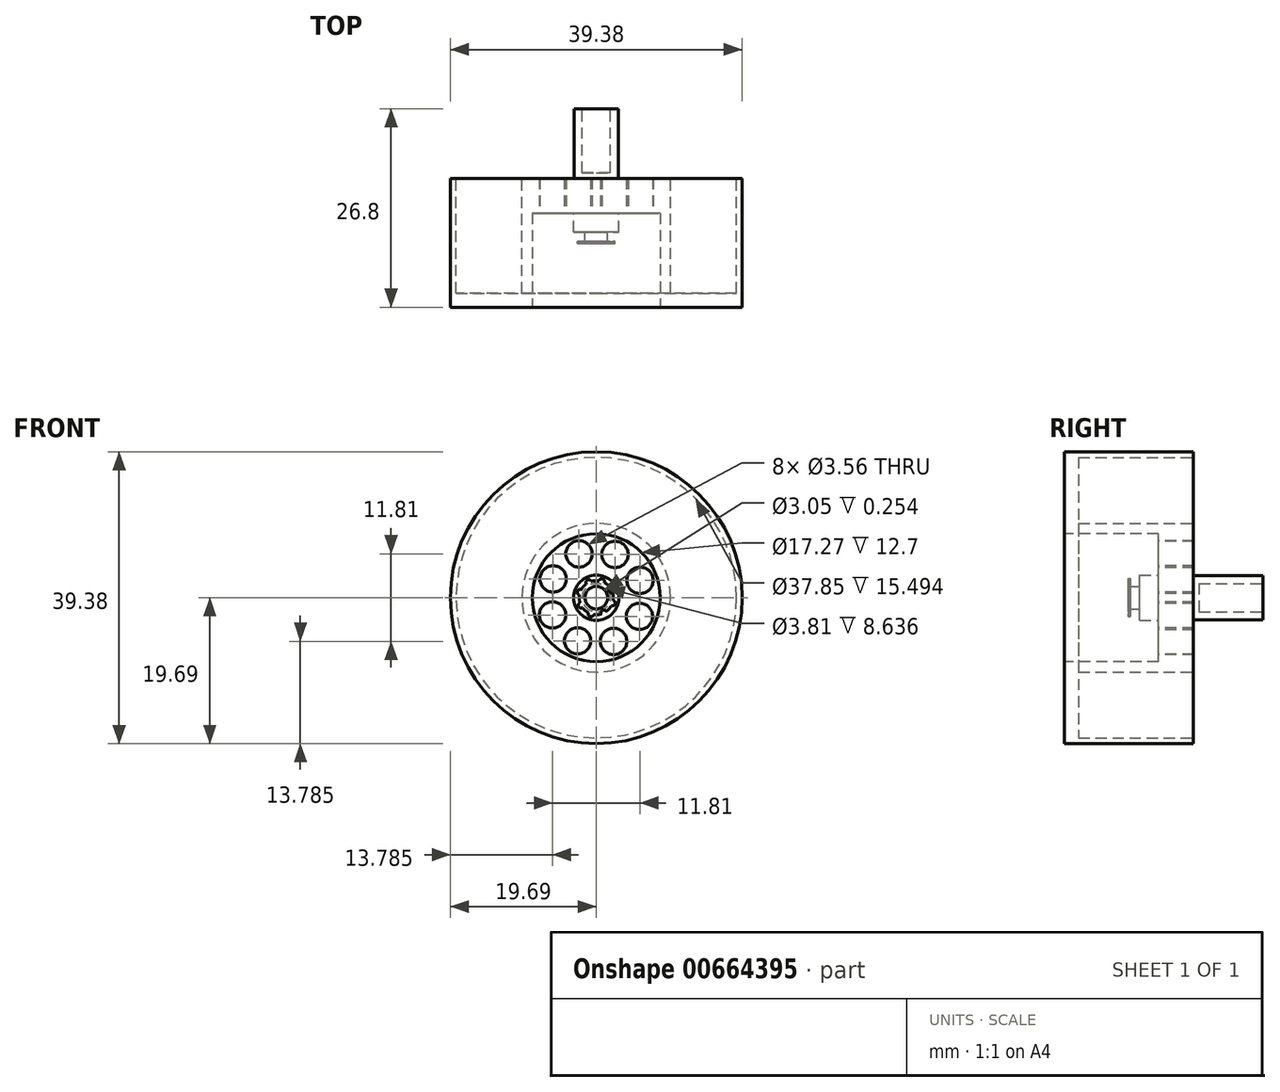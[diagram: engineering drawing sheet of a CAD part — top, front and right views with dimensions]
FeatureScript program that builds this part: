
annotation { "Feature Type Name" : "Feature", "Feature Type Description" : "" }
export const myFeature = defineFeature(function(context is Context, id is Id, definition is map)
    precondition{}
    {
        {
            var Q0;
            Q0=qCreatedBy(makeId("Front.planeOp"),FACE);
            var sketch = newSketch(context, id + "F0", { "sketchPlane" : qUnion([Q0])});
            skCircle(sketch, "E0", {"center": v(0, 0) * mm, "radius": 19.69 * mm});
            skSolve(sketch);
        }
        {
            var Q0;
            Q0 = qSketchRegion(id + "F0", true);
            extrude(context, id + "F1", {"entities" : qUnion([Q0]), "oppositeDirection" : true, "depth" : 17.4 * mm, "offsetDistance" : 25.4 * mm});
        }
        {
            var Q0;
            Q0=qCreatedBy(makeId("Front.planeOp"),FACE);
            var sketch = newSketch(context, id + "F2", { "sketchPlane" : qUnion([Q0])});
            skCircle(sketch, "E1", {"center": v(0, 0) * mm, "radius": 7.62 * mm});
            skSolve(sketch);
        }
        {
            var Q0;
            Q0 = qSketchRegion(id + "F2", true);
            extrude(context, id + "F3", {"entities" : qUnion([Q0]), "operationType" : NewBodyOperationType.REMOVE, "oppositeDirection" : true, "depth" : 13.2 * mm, "offsetDistance" : 25.4 * mm});
        }
        {
            var Q0;
            Q0 = qSketchRegion(id + "F0", true);
            extrude(context, id + "F4", {"entities" : qUnion([Q0]), "operationType" : NewBodyOperationType.ADD, "oppositeDirection" : true, "depth" : 16.5 * mm, "offsetDistance" : 25.4 * mm});
        }
        {
            var Q0;
            {var subQ0=sQuery(id+"F0.wireOp",EDGE,"E0");Q0=makeQuery(id+"F4.boolean.opBoolean","MERGE",FACE,{"derivedFrom":[makeQuery(id+"F1.opExtrude","CAP_FACE",FACE,{"disambiguationData":[OSD([subQ0])],"isStart":true}),makeQuery(id+"F4.opExtrude","CAP_FACE",FACE,{"disambiguationData":[OSD([subQ0])],"isStart":true})]});}
            var sketch = newSketch(context, id + "F5", { "sketchPlane" : qUnion([Q0])});
            skCircle(sketch, "E2", {"center": v(0, 0) * mm, "radius": 8.64 * mm});
            skSolve(sketch);
        }
        {
            var Q0;
            Q0 = qSketchRegion(id + "F5", true);
            extrude(context, id + "F6", {"entities" : qUnion([Q0]), "operationType" : NewBodyOperationType.REMOVE, "oppositeDirection" : true, "depth" : 12.7 * mm, "offsetDistance" : 25.4 * mm});
        }
        {
            var Q0;
            Q0=makeQuery(id+"F6.boolean.opBoolean","COPY",FACE,{"derivedFrom":makeQuery(id+"F6.opExtrude","CAP_FACE",FACE,{"disambiguationData":[OSD([sQuery(id+"F5.wireOp",EDGE,"E2")])],"isStart":false})});
            var sketch = newSketch(context, id + "F7", { "sketchPlane" : qUnion([Q0])});
            skCircle(sketch, "E3", {"center": v(0, 0) * mm, "radius": 3.05 * mm});
            skSolve(sketch);
        }
        {
            var Q0;
            Q0 = qSketchRegion(id + "F7", true);
            extrude(context, id + "F8", {"entities" : qUnion([Q0]), "operationType" : NewBodyOperationType.ADD, "depth" : 2.54 * mm, "offsetDistance" : 25.4 * mm});
        }
        {
            var Q0;
            Q0=makeQuery(id+"F8.opExtrude","CAP_FACE",FACE,{"disambiguationData":[OSD([sQuery(id+"F7.wireOp",EDGE,"E3")])],"isStart":false});
            var sketch = newSketch(context, id + "F9", { "sketchPlane" : qUnion([Q0])});
            skCircle(sketch, "E4", {"center": v(0, 0) * mm, "radius": 1.52 * mm});
            skSolve(sketch);
        }
        {
            var Q0;
            Q0 = qSketchRegion(id + "F9", true);
            extrude(context, id + "F10", {"entities" : qUnion([Q0]), "operationType" : NewBodyOperationType.ADD, "depth" : 1.27 * mm, "offsetDistance" : 25.4 * mm});
        }
        {
            var Q0;
            Q0=makeQuery(id+"F10.opExtrude","CAP_FACE",FACE,{"disambiguationData":[OSD([sQuery(id+"F9.wireOp",EDGE,"E4")])],"isStart":false});
            var sketch = newSketch(context, id + "F11", { "sketchPlane" : qUnion([Q0])});
            skCircle(sketch, "E5", {"center": v(0, 0) * mm, "radius": 2.3 * mm});
            skCircle(sketch, "E6", {"center": v(-1.03, 2.06) * mm, "radius": 0.38 * mm});
            skCircle(sketch, "E7.1.0", {"center": v(-2.18, 0.73) * mm, "radius": 0.38 * mm});
            skCircle(sketch, "E7.2.0", {"center": v(-2.06, -1.03) * mm, "radius": 0.38 * mm});
            skCircle(sketch, "E7.3.0", {"center": v(-0.73, -2.18) * mm, "radius": 0.38 * mm});
            skCircle(sketch, "E7.4.0", {"center": v(1.03, -2.06) * mm, "radius": 0.38 * mm});
            skCircle(sketch, "E7.5.0", {"center": v(2.18, -0.73) * mm, "radius": 0.38 * mm});
            skCircle(sketch, "E7.6.0", {"center": v(2.06, 1.03) * mm, "radius": 0.38 * mm});
            skCircle(sketch, "E7.7.0", {"center": v(0.73, 2.18) * mm, "radius": 0.38 * mm});
            skSolve(sketch);
        }
        {
            var Q0;
            {var subQ0=sQuery(id+"F11.wireOp",EDGE,"E7.6.0");var subQ1=sQuery(id+"F11.wireOp",EDGE,"E5");var subQ2=makeQuery(id+"F11.imprint","INTERSECT",VERTEX,{"disambiguationData":[OD(0.0)],"derivedFrom":[subQ1,subQ0]});Q0=makeQuery(id+"F11.imprint","IMPRINT",FACE,{"disambiguationData":[TD([[makeQuery(id+"F11.imprint","IMPRINT",EDGE,{"disambiguationData":[TD([[subQ2,1.0]])],"derivedFrom":subQ1}),-1.0]])]});}
            var Q1;
            {var subQ0=sQuery(id+"F11.wireOp",EDGE,"E7.7.0");var subQ1=sQuery(id+"F11.wireOp",EDGE,"E5");var subQ2=makeQuery(id+"F11.imprint","INTERSECT",VERTEX,{"disambiguationData":[OD(0.0)],"derivedFrom":[subQ1,subQ0]});Q1=makeQuery(id+"F11.imprint","IMPRINT",FACE,{"disambiguationData":[TD([[makeQuery(id+"F11.imprint","IMPRINT",EDGE,{"disambiguationData":[TD([[subQ2,-1.0]])],"derivedFrom":subQ1}),-1.0]])]});}
            var Q2;
            {var subQ0=sQuery(id+"F11.wireOp",EDGE,"E6");var subQ1=sQuery(id+"F11.wireOp",EDGE,"E5");var subQ2=makeQuery(id+"F11.imprint","INTERSECT",VERTEX,{"disambiguationData":[OD(0.0)],"derivedFrom":[subQ1,subQ0]});Q2=makeQuery(id+"F11.imprint","IMPRINT",FACE,{"disambiguationData":[TD([[makeQuery(id+"F11.imprint","IMPRINT",EDGE,{"disambiguationData":[TD([[subQ2,-1.0]])],"derivedFrom":subQ1}),-1.0]])]});}
            var Q3;
            {var subQ0=sQuery(id+"F11.wireOp",EDGE,"E7.1.0");var subQ1=sQuery(id+"F11.wireOp",EDGE,"E5");var subQ2=makeQuery(id+"F11.imprint","INTERSECT",VERTEX,{"disambiguationData":[OD(0.0)],"derivedFrom":[subQ1,subQ0]});Q3=makeQuery(id+"F11.imprint","IMPRINT",FACE,{"disambiguationData":[TD([[makeQuery(id+"F11.imprint","IMPRINT",EDGE,{"disambiguationData":[TD([[subQ2,-1.0]])],"derivedFrom":subQ1}),-1.0]])]});}
            var Q4;
            {var subQ0=sQuery(id+"F11.wireOp",EDGE,"E7.2.0");var subQ1=sQuery(id+"F11.wireOp",EDGE,"E5");var subQ2=makeQuery(id+"F11.imprint","INTERSECT",VERTEX,{"disambiguationData":[OD(0.0)],"derivedFrom":[subQ1,subQ0]});Q4=makeQuery(id+"F11.imprint","IMPRINT",FACE,{"disambiguationData":[TD([[makeQuery(id+"F11.imprint","IMPRINT",EDGE,{"disambiguationData":[TD([[subQ2,-1.0]])],"derivedFrom":subQ1}),-1.0]])]});}
            var Q5;
            {var subQ0=sQuery(id+"F11.wireOp",EDGE,"E7.3.0");var subQ1=sQuery(id+"F11.wireOp",EDGE,"E5");var subQ2=makeQuery(id+"F11.imprint","INTERSECT",VERTEX,{"disambiguationData":[OD(0.0)],"derivedFrom":[subQ1,subQ0]});Q5=makeQuery(id+"F11.imprint","IMPRINT",FACE,{"disambiguationData":[TD([[makeQuery(id+"F11.imprint","IMPRINT",EDGE,{"disambiguationData":[TD([[subQ2,-1.0]])],"derivedFrom":subQ1}),-1.0]])]});}
            var Q6;
            {var subQ0=sQuery(id+"F11.wireOp",EDGE,"E7.4.0");var subQ1=sQuery(id+"F11.wireOp",EDGE,"E5");var subQ2=makeQuery(id+"F11.imprint","INTERSECT",VERTEX,{"disambiguationData":[OD(0.0)],"derivedFrom":[subQ1,subQ0]});Q6=makeQuery(id+"F11.imprint","IMPRINT",FACE,{"disambiguationData":[TD([[makeQuery(id+"F11.imprint","IMPRINT",EDGE,{"disambiguationData":[TD([[subQ2,-1.0]])],"derivedFrom":subQ1}),-1.0]])]});}
            var Q7;
            {var subQ0=sQuery(id+"F11.wireOp",EDGE,"E7.5.0");var subQ1=sQuery(id+"F11.wireOp",EDGE,"E5");var subQ2=makeQuery(id+"F11.imprint","INTERSECT",VERTEX,{"disambiguationData":[OD(0.0)],"derivedFrom":[subQ1,subQ0]});Q7=makeQuery(id+"F11.imprint","IMPRINT",FACE,{"disambiguationData":[TD([[makeQuery(id+"F11.imprint","IMPRINT",EDGE,{"disambiguationData":[TD([[subQ2,-1.0]])],"derivedFrom":subQ1}),-1.0]])]});}
            var Q8;
            {var subQ0=sQuery(id+"F11.wireOp",EDGE,"E7.6.0");var subQ1=sQuery(id+"F11.wireOp",EDGE,"E5");var subQ2=makeQuery(id+"F11.imprint","INTERSECT",VERTEX,{"disambiguationData":[OD(0.0)],"derivedFrom":[subQ1,subQ0]});Q8=makeQuery(id+"F11.imprint","IMPRINT",FACE,{"disambiguationData":[TD([[makeQuery(id+"F11.imprint","IMPRINT",EDGE,{"disambiguationData":[TD([[subQ2,1.0]])],"derivedFrom":subQ1}),1.0]])]});}
            var Q9;
            {var subQ0=sQuery(id+"F11.wireOp",EDGE,"E7.7.0");var subQ1=sQuery(id+"F11.wireOp",EDGE,"E5");var subQ2=makeQuery(id+"F11.imprint","INTERSECT",VERTEX,{"disambiguationData":[OD(0.0)],"derivedFrom":[subQ1,subQ0]});Q9=makeQuery(id+"F11.imprint","IMPRINT",FACE,{"disambiguationData":[TD([[makeQuery(id+"F11.imprint","IMPRINT",EDGE,{"disambiguationData":[TD([[subQ2,-1.0]])],"derivedFrom":subQ1}),1.0]])]});}
            var Q10;
            {var subQ0=sQuery(id+"F11.wireOp",EDGE,"E6");var subQ1=sQuery(id+"F11.wireOp",EDGE,"E5");var subQ2=makeQuery(id+"F11.imprint","INTERSECT",VERTEX,{"disambiguationData":[OD(0.0)],"derivedFrom":[subQ1,subQ0]});Q10=makeQuery(id+"F11.imprint","IMPRINT",FACE,{"disambiguationData":[TD([[makeQuery(id+"F11.imprint","IMPRINT",EDGE,{"disambiguationData":[TD([[subQ2,-1.0]])],"derivedFrom":subQ1}),1.0]])]});}
            var Q11;
            {var subQ0=sQuery(id+"F11.wireOp",EDGE,"E7.1.0");var subQ1=sQuery(id+"F11.wireOp",EDGE,"E5");var subQ2=makeQuery(id+"F11.imprint","INTERSECT",VERTEX,{"disambiguationData":[OD(0.0)],"derivedFrom":[subQ1,subQ0]});Q11=makeQuery(id+"F11.imprint","IMPRINT",FACE,{"disambiguationData":[TD([[makeQuery(id+"F11.imprint","IMPRINT",EDGE,{"disambiguationData":[TD([[subQ2,-1.0]])],"derivedFrom":subQ1}),1.0]])]});}
            var Q12;
            {var subQ0=sQuery(id+"F11.wireOp",EDGE,"E7.2.0");var subQ1=sQuery(id+"F11.wireOp",EDGE,"E5");var subQ2=makeQuery(id+"F11.imprint","INTERSECT",VERTEX,{"disambiguationData":[OD(0.0)],"derivedFrom":[subQ1,subQ0]});Q12=makeQuery(id+"F11.imprint","IMPRINT",FACE,{"disambiguationData":[TD([[makeQuery(id+"F11.imprint","IMPRINT",EDGE,{"disambiguationData":[TD([[subQ2,-1.0]])],"derivedFrom":subQ1}),1.0]])]});}
            var Q13;
            {var subQ0=sQuery(id+"F11.wireOp",EDGE,"E7.3.0");var subQ1=sQuery(id+"F11.wireOp",EDGE,"E5");var subQ2=makeQuery(id+"F11.imprint","INTERSECT",VERTEX,{"disambiguationData":[OD(0.0)],"derivedFrom":[subQ1,subQ0]});Q13=makeQuery(id+"F11.imprint","IMPRINT",FACE,{"disambiguationData":[TD([[makeQuery(id+"F11.imprint","IMPRINT",EDGE,{"disambiguationData":[TD([[subQ2,-1.0]])],"derivedFrom":subQ1}),1.0]])]});}
            var Q14;
            {var subQ0=sQuery(id+"F11.wireOp",EDGE,"E7.4.0");var subQ1=sQuery(id+"F11.wireOp",EDGE,"E5");var subQ2=makeQuery(id+"F11.imprint","INTERSECT",VERTEX,{"disambiguationData":[OD(0.0)],"derivedFrom":[subQ1,subQ0]});Q14=makeQuery(id+"F11.imprint","IMPRINT",FACE,{"disambiguationData":[TD([[makeQuery(id+"F11.imprint","IMPRINT",EDGE,{"disambiguationData":[TD([[subQ2,-1.0]])],"derivedFrom":subQ1}),1.0]])]});}
            var Q15;
            {var subQ0=sQuery(id+"F11.wireOp",EDGE,"E7.5.0");var subQ1=sQuery(id+"F11.wireOp",EDGE,"E5");var subQ2=makeQuery(id+"F11.imprint","INTERSECT",VERTEX,{"disambiguationData":[OD(0.0)],"derivedFrom":[subQ1,subQ0]});Q15=makeQuery(id+"F11.imprint","IMPRINT",FACE,{"disambiguationData":[TD([[makeQuery(id+"F11.imprint","IMPRINT",EDGE,{"disambiguationData":[TD([[subQ2,-1.0]])],"derivedFrom":subQ1}),1.0]])]});}
            extrude(context, id + "F12", {"entities" : qUnion([Q0, Q1, Q2, Q3, Q4, Q5, Q6, Q7, Q8, Q9, Q10, Q11, Q12, Q13, Q14, Q15]), "depth" : 0.25 * mm, "offsetDistance" : 25.4 * mm});
        }
        {
            var Q0;
            Q0=makeQuery(id+"F6.boolean.opBoolean","COPY",FACE,{"derivedFrom":makeQuery(id+"F6.opExtrude","CAP_FACE",FACE,{"disambiguationData":[OSD([sQuery(id+"F5.wireOp",EDGE,"E2")])],"isStart":false})});
            var sketch = newSketch(context, id + "F13", { "sketchPlane" : qUnion([Q0])});
            skCircle(sketch, "E8", {"center": v(-2.34, 5.9) * mm, "radius": 1.78 * mm});
            skCircle(sketch, "E9.1.0", {"center": v(-5.83, 2.52) * mm, "radius": 1.78 * mm});
            skCircle(sketch, "E9.2.0", {"center": v(-5.9, -2.34) * mm, "radius": 1.78 * mm});
            skCircle(sketch, "E9.3.0", {"center": v(-2.52, -5.83) * mm, "radius": 1.78 * mm});
            skCircle(sketch, "E9.4.0", {"center": v(2.34, -5.9) * mm, "radius": 1.78 * mm});
            skCircle(sketch, "E9.5.0", {"center": v(5.83, -2.52) * mm, "radius": 1.78 * mm});
            skCircle(sketch, "E9.6.0", {"center": v(5.9, 2.34) * mm, "radius": 1.78 * mm});
            skCircle(sketch, "E9.7.0", {"center": v(2.52, 5.83) * mm, "radius": 1.78 * mm});
            skPoint(sketch, "E9.center", {"position": v(0, 0) * mm});
            skSolve(sketch);
        }
        {
            var Q0;
            Q0 = qSketchRegion(id + "F13", true);
            extrude(context, id + "F14", {"entities" : qUnion([Q0]), "operationType" : NewBodyOperationType.REMOVE, "oppositeDirection" : true, "depth" : 25.4 * mm, "offsetDistance" : 25.4 * mm});
        }
        {
            var Q0;
            Q0=makeQuery(id+"F1.opExtrude","CAP_FACE",FACE,{"disambiguationData":[OSD([sQuery(id+"F0.wireOp",EDGE,"E0")])],"isStart":false});
            var sketch = newSketch(context, id + "F15", { "sketchPlane" : qUnion([Q0])});
            skCircle(sketch, "E10", {"center": v(0, 0) * mm, "radius": 18.92 * mm});
            skCircle(sketch, "E11", {"center": v(0, 0) * mm, "radius": 10.03 * mm});
            skSolve(sketch);
        }
        {
            var Q0;
            Q0 = qSketchRegion(id + "F15", true);
            extrude(context, id + "F16", {"entities" : qUnion([Q0]), "operationType" : NewBodyOperationType.REMOVE, "oppositeDirection" : true, "depth" : 15.5 * mm, "offsetDistance" : 25.4 * mm});
        }
        {
            var Q0;
            Q0=makeQuery(id+"F16.boolean.opBoolean","SPLIT",FACE,{"disambiguationData":[TD([makeQuery(id+"F14.boolean.opBoolean","COPY",FACE,{"derivedFrom":makeQuery(id+"F14.opExtrude","SWEPT_FACE",FACE,{"disambiguationData":[OSD([sQuery(id+"F13.wireOp",EDGE,"E8")])]})})])],"derivedFrom":makeQuery(id+"F1.opExtrude","CAP_FACE",FACE,{"disambiguationData":[OSD([sQuery(id+"F0.wireOp",EDGE,"E0")])],"isStart":false})});
            var sketch = newSketch(context, id + "F17", { "sketchPlane" : qUnion([Q0])});
            skCircle(sketch, "E12", {"center": v(0, 0) * mm, "radius": 3 * mm});
            skSolve(sketch);
        }
        {
            var Q0;
            Q0 = qSketchRegion(id + "F17", true);
            extrude(context, id + "F18", {"entities" : qUnion([Q0]), "operationType" : NewBodyOperationType.ADD, "depth" : 9.4 * mm, "offsetDistance" : 25.4 * mm});
        }
        {
            var Q0;
            Q0=makeQuery(id+"F18.opExtrude","CAP_FACE",FACE,{"disambiguationData":[OSD([sQuery(id+"F17.wireOp",EDGE,"E12")])],"isStart":false});
            var sketch = newSketch(context, id + "F19", { "sketchPlane" : qUnion([Q0])});
            skCircle(sketch, "E13", {"center": v(0, 0) * mm, "radius": 1.9 * mm});
            skSolve(sketch);
        }
        {
            var Q0;
            Q0 = qSketchRegion(id + "F19", true);
            extrude(context, id + "F20", {"entities" : qUnion([Q0]), "operationType" : NewBodyOperationType.REMOVE, "oppositeDirection" : true, "depth" : 8.64 * mm, "offsetDistance" : 25.4 * mm});
        }
    });
